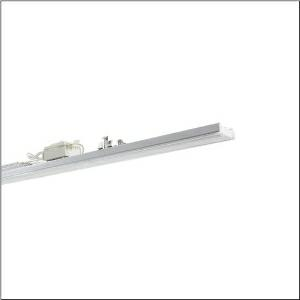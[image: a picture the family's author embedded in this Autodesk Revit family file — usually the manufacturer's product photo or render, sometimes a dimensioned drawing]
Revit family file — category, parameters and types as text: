
# Revit family: licross_r__21_recessed_mo_52tl187n485g_8ad4
name_source: partatom
category: Lighting Fixtures
units: mm (PartAtom-declared; Revit-internal decimal feet)

## family parameters
Cut with Voids When Loaded = No
Host = Face
Light Source = No
Part Type = Normal
Room Calculation Point = No
Round Connector Dimension = Use Diameter
Shared = No

## types (1)
- Licross® 21 Recessed MO (1 x LED, 8570 lm, 47.9 W, 4000K)
    Apparent Load = 48 VA
    CIE Flux Codes = 79 95 99 100 100
    Color Rendering = 80
    Color Temperature = 4000K
    Default Elevation = 1800 mm
    Description = Licross® 21 Recessed MO, luminaire insert, of sheet steel, galvanised, coil coated, white, length: 1.500mm, width: 66mm, height: 67mm, LED rated luminous flux: 8.570lm, light colour: 840, control gear: ON/OFF, with plug, 3-pole, with phase selection, mains connection: 220..240V, AC, 50/60Hz, rated input power: 48W, internal wiring halogen-free, primary light control with lens, of plastic, primary optical cover: cover, of PMMA, light emission: direct distribution, primary light characteristic: symmetric, protection rating (complete): IP40, insulation class (complete): insulation class I (protective earthing), certification: CE, ENEC, VDE, UKCA, protection symbol: D if used in an environment without relevant dust loads with corresponding accessories, impact resistance: IK06, permissible ambient temperature for indoor applications: -35..+40°C, corresponds to IFS (International Featured Standards) requirements for safety and quality in the food industry, reducing of maximum allowable ambient temperature of 5°C with ceiling mounting, LABS conformity tested according to VDMA 24364:2018-05, packaging unit: 1 piece
    Height = 58 mm
    Lamp = 1 x LED
    Lamp Light Flux = 8570 lm
    Lamp Power = 47.9 W
    Lamp count = 1
    Length = 1500 mm
    Luminous efficacy = 179 lm/W
    Manufacturer = Siteco
    ModVariant = No
    Model = 52TL187N485G
    Mounting Place = Ceiling
    Mounting Type = Pendant
    Number of Poles = 1
    OnlyDefault = Yes
    Power Factor = 1
    Product Name = Licross® 21 Recessed MO
    Product group = luminaire insert | ceiling pendant
    ProductGroupID = 902
    Protection Class = Protection class I
    Protection Degree = IP 40
    RLX_Detail_Level = 1
    RLX_Emergency_Light_Flux = 0 lm
    RLX_Emergency_Type = 0
    RLX_Emergency_Type_DB = No
    RlxData = <blob elided: 20937 chars, md5=dfa24ee5>
    Socket = socket
    Standby Power = 0 W
    System Light Flux = 8570 lm
    System Power = 48 W
    Type Comments = Product without accessories
    Type Image = l_1296930.jpg
    URL = http://relux.com
    VarID = ---
    Voltage = 0 V
    Weight = 0.00 kg
    Width = 66 mm

## geometry (parser evidence)
native form markers: Blend x4, Sweep x10
no freeform markers — native parametric forms only
